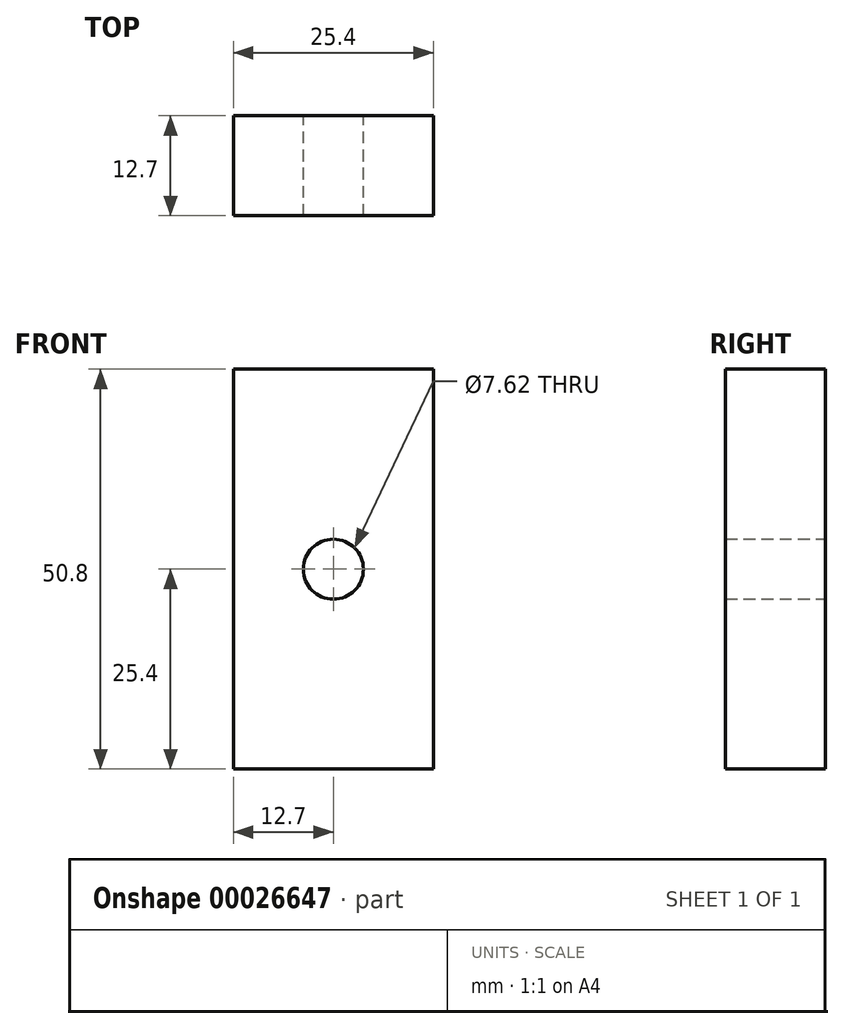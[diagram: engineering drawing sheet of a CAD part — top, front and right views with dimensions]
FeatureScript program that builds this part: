
annotation { "Feature Type Name" : "Feature", "Feature Type Description" : "" }
export const myFeature = defineFeature(function(context is Context, id is Id, definition is map)
    precondition{}
    {
        {
            var Q0;
            Q0=qCreatedBy(makeId("Front.planeOp"),FACE);
            var sketch = newSketch(context, id + "F0", { "sketchPlane" : qUnion([Q0])});
            skLineSegment(sketch, "E0.bottom", {"start": v(-10.47, 0) * mm, "end": v(14.93, 0) * mm});
            skLineSegment(sketch, "E0.top", {"start": v(-10.47, -50.8) * mm, "end": v(14.93, -50.8) * mm});
            skLineSegment(sketch, "E0.left", {"start": v(-10.47, 0) * mm, "end": v(-10.47, -50.8) * mm});
            skLineSegment(sketch, "E0.right", {"start": v(14.93, 0) * mm, "end": v(14.93, -50.8) * mm});
            skLineSegment(sketch, "E1", {"start": v(-10.47, 0) * mm, "end": v(14.93, -50.8) * mm});
            skCircle(sketch, "E2", {"center": v(2.23, -25.4) * mm, "radius": 3.81 * mm});
            skSolve(sketch);
        }
        {
            var Q0;
            {var subQ5=sQuery(id+"F0.wireOp",EDGE,"E0.bottom");Q0=makeQuery(id+"F0.imprint","IMPRINT",FACE,{"disambiguationData":[TD([[makeQuery(id+"F0.imprint","IMPRINT",EDGE,{"derivedFrom":subQ5}),-1.0]])]});}
            extrude(context, id + "F1", {"entities" : qUnion([Q0]), "depth" : 12.7 * mm});
        }
        {
            var Q0;
            {var subQ4=sQuery(id+"F0.wireOp",EDGE,"E0.top");Q0=makeQuery(id+"F0.imprint","IMPRINT",FACE,{"disambiguationData":[TD([[makeQuery(id+"F0.imprint","IMPRINT",EDGE,{"derivedFrom":subQ4}),1.0]])]});}
            extrude(context, id + "F2", {"entities" : qUnion([Q0]), "operationType" : NewBodyOperationType.ADD, "depth" : 12.7 * mm});
        }
    });
